# Revit family: Ifö Spira 15048 WB left - 415 mm
name_source: partatom
category: Generic Models
revit_build: Autodesk Revit 2015 (Build: 20140606_1530(x64)
units: mm (PartAtom-declared; Revit-internal decimal feet)

## types (1)
- Ifö Spira 15048 WB  left - 415 mm
    BIMObjectName = Ifö Spira 15048 WB left - 415 mm
    Brackets = Metal-Steel
    Brand = Ifö
    Category = WashHandBasin
    Color = White
    ConnectorIn_HDistance = 120.00 mm
    ConnectorIn_VDistance = 50.00 mm
    Depth = 310.00 mm
    Description = Ifö Spira 15048 Wash basin L, 41,5 cm
    DrainSize = 0.00 mm
    Features = feature1, feature2, feature7
    Finish = Glazed
    Height = 148.00 mm
    Manufacturer = Geberit
    Material = Porcelain
    Mixernotincluded(option) = Yes
    Model = Ifö Spira 15048 WB 415 mm left
    ModelNumber = 15048
    ModelReference = Spira
    MountingHeight(offset) = 850.00 mm
    Name = Ifö Spira 15048 Wash basin L, 41,5 cm
    NominalDepth = 310.00 mm
    NominalHeight = 148.00 mm
    NominalWidth = 415.00 mm
    ReturnPipeDiameter = 32.00 mm
    Serie = Spira
    Shape = Rounded
    Size = 415x148x310
    SupplyPipeDiameter = 10.00 mm
    Type = Building element
    URL.dk = http://www.ifo.dk
    URL.no = http://www.ifosanitar.no
    URL.se = http://www.ifo.se
    WashHandBasinType = Vanity
    WashHandBasingMounting = WallHung
    Width = 415.00 mm
    ifcExportAs = ifcSanitaryTerminalType
    ifcExportType = WASHHANDBASIN

## geometry (parser evidence)
native form markers: Blend x4, Sweep x6
no freeform markers — native parametric forms only
